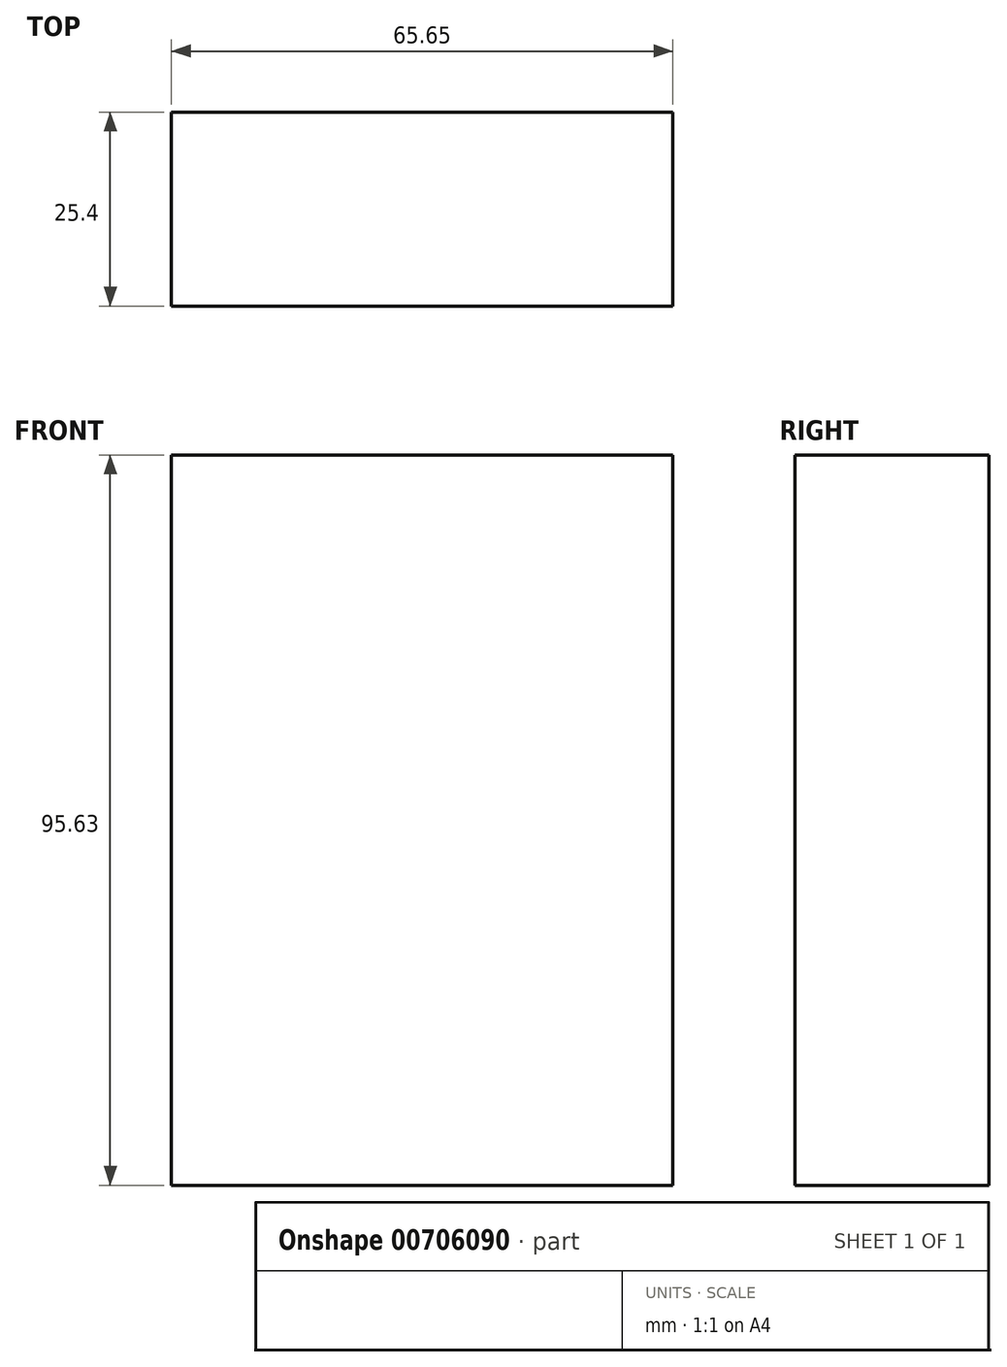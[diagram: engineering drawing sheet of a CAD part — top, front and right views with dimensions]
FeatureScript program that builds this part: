
annotation { "Feature Type Name" : "Feature", "Feature Type Description" : "" }
export const myFeature = defineFeature(function(context is Context, id is Id, definition is map)
    precondition{}
    {
        {
            var Q0;
            Q0=qCreatedBy(makeId("Front.planeOp"),FACE);
            var sketch = newSketch(context, id + "F0", { "sketchPlane" : qUnion([Q0])});
            skLineSegment(sketch, "E0.bottom", {"start": v(-32.18, 61.09) * mm, "end": v(33.47, 61.09) * mm});
            skLineSegment(sketch, "E0.top", {"start": v(-32.18, -34.54) * mm, "end": v(33.47, -34.54) * mm});
            skLineSegment(sketch, "E0.left", {"start": v(-32.18, 61.09) * mm, "end": v(-32.18, -34.54) * mm});
            skLineSegment(sketch, "E0.right", {"start": v(33.47, 61.09) * mm, "end": v(33.47, -34.54) * mm});
            skSolve(sketch);
        }
        {
            var Q0;
            Q0 = qSketchRegion(id + "F0", true);
            extrude(context, id + "F1", {"entities" : qUnion([Q0]), "depth" : 25.4 * mm, "offsetDistance" : 25.4 * mm});
        }
    });
